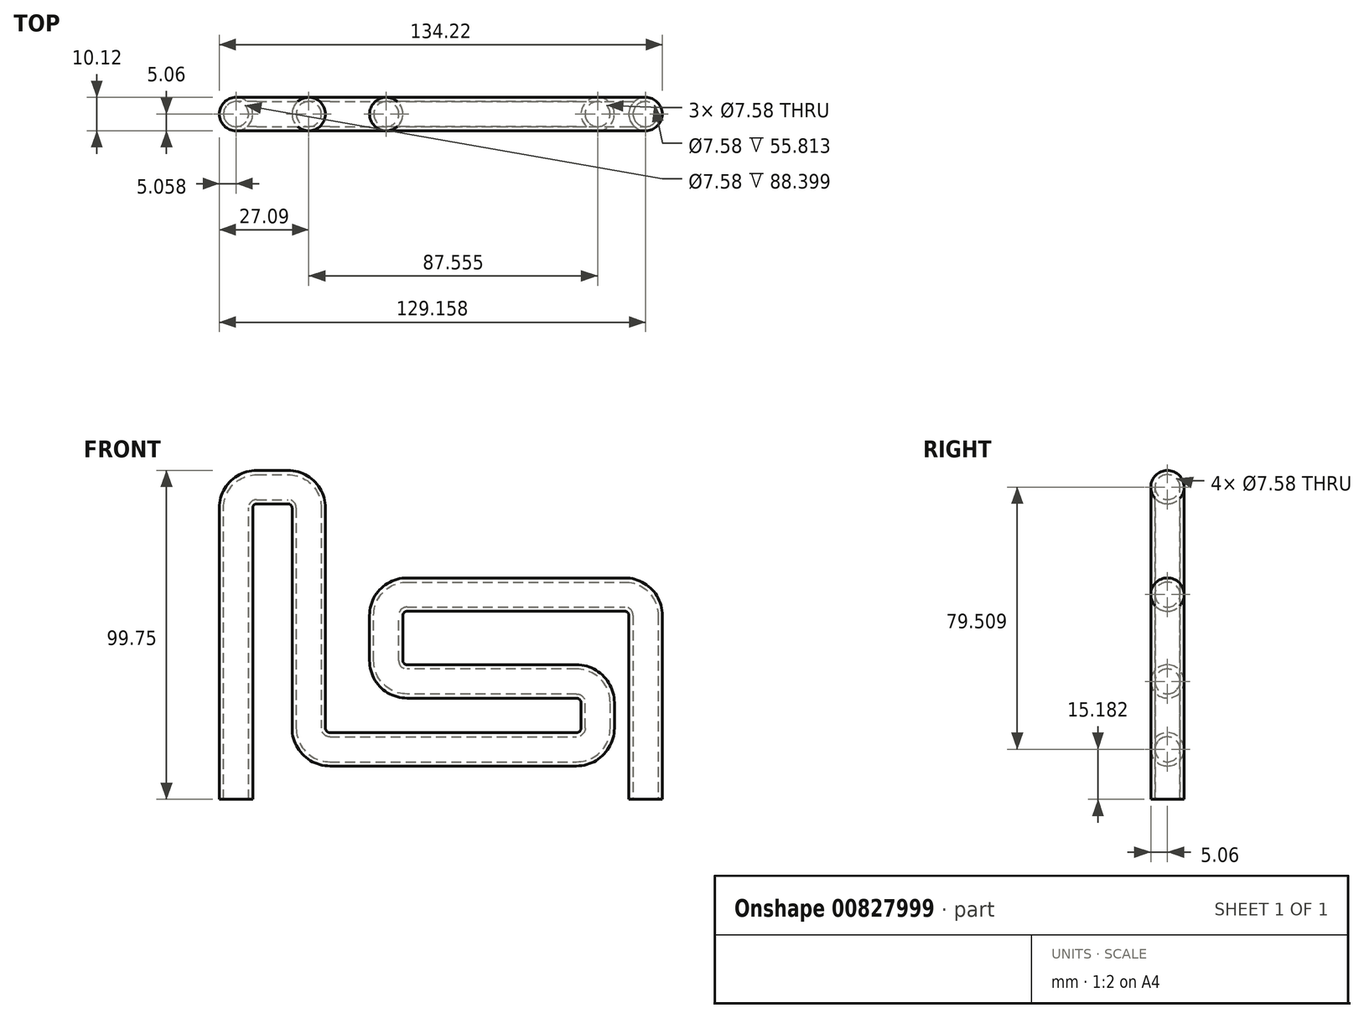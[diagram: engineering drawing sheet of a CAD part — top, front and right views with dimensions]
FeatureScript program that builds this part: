
annotation { "Feature Type Name" : "Feature", "Feature Type Description" : "" }
export const myFeature = defineFeature(function(context is Context, id is Id, definition is map)
    precondition{}
    {
        {
            var Q0;
            Q0=qCreatedBy(makeId("Front.planeOp"),FACE);
            var sketch = newSketch(context, id + "F0", { "sketchPlane" : qUnion([Q0])});
            skLineSegment(sketch, "E0", {"start": v(-59.1, -51.59) * mm, "end": v(-59.1, 36.81) * mm});
            skLineSegment(sketch, "E1", {"start": v(-52.76, 43.16) * mm, "end": v(-43.3, 43.16) * mm});
            skLineSegment(sketch, "E2", {"start": v(-36.95, 36.81) * mm, "end": v(-36.95, -30) * mm});
            skLineSegment(sketch, "E3", {"start": v(-30.6, -36.35) * mm, "end": v(44.13, -36.35) * mm});
            skLineSegment(sketch, "E4", {"start": v(50.48, -30) * mm, "end": v(50.48, -22.24) * mm});
            skLineSegment(sketch, "E5", {"start": v(44.13, -15.9) * mm, "end": v(-7.24, -15.9) * mm});
            skLineSegment(sketch, "E6", {"start": v(-13.59, -9.54) * mm, "end": v(-13.59, 4.23) * mm});
            skLineSegment(sketch, "E7", {"start": v(-7.24, 10.58) * mm, "end": v(58.77, 10.58) * mm});
            skLineSegment(sketch, "E8", {"start": v(65.12, 4.23) * mm, "end": v(65.12, -51.59) * mm});
            skPoint(sketch, "E9.visualSharp", {"position": v(-59.1, 43.16) * mm});
            skArc(sketch, "E9.filletArc", {"start": v(-52.76, 43.16) * mm, "mid": v(-57.25, 41.3) * mm, "end": v(-59.1, 36.81) * mm});
            skPoint(sketch, "E10.visualSharp", {"position": v(-36.95, 43.16) * mm});
            skArc(sketch, "E10.filletArc", {"start": v(-36.95, 36.81) * mm, "mid": v(-38.8, 41.3) * mm, "end": v(-43.3, 43.16) * mm});
            skPoint(sketch, "E11.visualSharp", {"position": v(-36.95, -36.35) * mm});
            skArc(sketch, "E11.filletArc", {"start": v(-36.95, -30) * mm, "mid": v(-35.09, -34.49) * mm, "end": v(-30.6, -36.35) * mm});
            skPoint(sketch, "E12.visualSharp", {"position": v(50.48, -36.35) * mm});
            skArc(sketch, "E12.filletArc", {"start": v(44.13, -36.35) * mm, "mid": v(48.62, -34.49) * mm, "end": v(50.48, -30) * mm});
            skPoint(sketch, "E13.visualSharp", {"position": v(50.48, -15.9) * mm});
            skArc(sketch, "E13.filletArc", {"start": v(50.48, -22.24) * mm, "mid": v(48.62, -17.75) * mm, "end": v(44.13, -15.9) * mm});
            skPoint(sketch, "E14.visualSharp", {"position": v(-13.59, -15.9) * mm});
            skArc(sketch, "E14.filletArc", {"start": v(-13.59, -9.54) * mm, "mid": v(-11.73, -14.03) * mm, "end": v(-7.24, -15.9) * mm});
            skPoint(sketch, "E15.visualSharp", {"position": v(-13.59, 10.58) * mm});
            skArc(sketch, "E15.filletArc", {"start": v(-7.24, 10.58) * mm, "mid": v(-11.73, 8.72) * mm, "end": v(-13.59, 4.23) * mm});
            skPoint(sketch, "E16.visualSharp", {"position": v(65.12, 10.58) * mm});
            skArc(sketch, "E16.filletArc", {"start": v(65.12, 4.23) * mm, "mid": v(63.26, 8.72) * mm, "end": v(58.77, 10.58) * mm});
            skSolve(sketch);
        }
        {
            var Q0;
            Q0=sQuery(id+"F0.wireOp",VERTEX,"E0.start");
            var Q1;
            Q1=sQuery(id+"F0.wireOp",EDGE,"E0");
            cPlane(context, id + "F1", {"entities" : qUnion([Q0, Q1]), "cplaneType" : CPlaneType.LINE_POINT, "offset" : 25.4 * mm, "width" : 152.4 * mm, "height" : 152.4 * mm});
        }
        {
            var Q0;
            Q0=qCreatedBy(id+"F1.planeOp",FACE);
            var sketch = newSketch(context, id + "F2", { "sketchPlane" : qUnion([Q0])});
            skCircle(sketch, "E17", {"center": v(-59.04, 0) * mm, "radius": 5.06 * mm});
            skSolve(sketch);
        }
        {
            var Q0;
            Q0=makeQuery(id+"F2.imprint","IMPRINT",FACE,{"disambiguationData":[TD([[makeQuery(id+"F2.imprint","IMPRINT",EDGE,{"derivedFrom":sQuery(id+"F2.wireOp",EDGE,"E17")}),1.0]])]});
            var Q1;
            Q1 = qConstructionFilter(qBodyType(qCreatedBy(id + "F0" ,EDGE), BodyType.WIRE), ConstructionObject.NO);
            sweep(context, id + "F3", {"profiles" : qUnion([Q0]), "path" : qUnion([Q1])});
        }
        {
            var Q0;
            Q0=makeQuery(id+"F3.opSweep","CAP_FACE",FACE,{"disambiguationData":[OSD([sQuery(id+"F0.wireOp",VERTEX,"E0.start"),sQuery(id+"F2.wireOp",EDGE,"E17")])],"isStart":true});
            var Q1;
            Q1=makeQuery(id+"F3.opSweep","CAP_FACE",FACE,{"disambiguationData":[OSD([sQuery(id+"F0.wireOp",VERTEX,"E8.end"),sQuery(id+"F2.wireOp",EDGE,"E17")])],"isStart":false});
            shell(context, id + "F4", {"entities" : qUnion([Q0, Q1]), "thickness" : 1.27 * mm});
        }
    });
